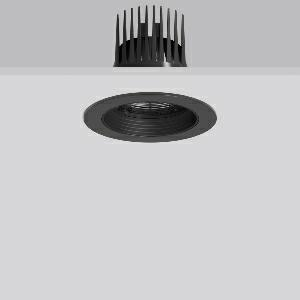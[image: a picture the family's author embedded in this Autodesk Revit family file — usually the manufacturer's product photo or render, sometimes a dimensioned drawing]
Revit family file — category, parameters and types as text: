
# Revit family: heledon_maxi_e_901768_003_2_8095
name_source: partatom
category: Lighting Fixtures
units: mm (PartAtom-declared; Revit-internal decimal feet)

## family parameters
Cut with Voids When Loaded = No
Host = Face
Light Source = No
Part Type = Normal
Room Calculation Point = No
Round Connector Dimension = Use Diameter
Shared = No

## types (1)
- HELEDON maxi E (1 x LED Modul 927, 3350 lm, 2700)
    Apparent Load = 35 VA
    Approval mark = CE
    CIE Flux Codes = 96 100 100 100 100
    Color Rendering = 92
    Color Temperature = 2700
    Default Elevation = 1800 mm
    Description = Series: HELEDON maxi
Round recessed downlight. Housing: die-cast aluminium, powder-coated. Black plastic ring and recessed LED to prevent glare from the side. Optical assembly with lens made of plastic (polycarbonate) for the best homogeneous light distribution - can be changed without tools. Best colour rendering index Ra>90. Suitable for Recessed ceiling mounting. Installation without tools thanks to spring fastening system. Including separate LED converter with connecting cable 600 mm.High quality converter without flickering and stroboscopic effect. Through-wiring box (5 pole) available as accessory. The following accessories can be mounted without use of tools: interchangeable lenses, decorative glasses, honeycomb louvre, clear and frosted diffusers, white interchangeable plastic ring. 
Colour: deep black, matt (RAL 9005)
Diameter: 162 mm
Height: 3 mm
Cut-out diameter: 152 mm
Recess height: 200 mm
Luminaire: recess height: 135 mm
Lamp: LED
Socket: without socket
Colour temperature: 2700K
Colour rendering index (CRI): 92
System power: 35 W
Rated luminous flux: 3350 lm
Luminous efficiency: 96 lm/W
Control gear: Regulated power supply
Protection class: II
Type of protection: IP 20
    Height = 0 mm  [stored 0 ft]
    Lamp = 1 x LED Modul 927
    Lamp Light Flux = 3350 lm
    Lamp count = 1
    Length = 162 mm
    Lifetime = 50000 h
    Luminous efficacy = 96 lm/W
    Manufacturer = RZB
    ModVariant = No
    Model = 901768.003.2
    Mounting Place = Ceiling
    Mounting Type = Recessed
    Number of Poles = 1
    OnlyDefault = Yes
    Power Factor = 1
    Product Name = HELEDON maxi E
    Product group = Recessed downlights
    ProductGroupID = 402
    Protection Class = Protection class II
    Protection Degree = IP 20
    RLX_Detail_Level = 1
    RLX_Emergency_Light_Flux = 0 lm
    RLX_Emergency_Type = 0
    RLX_Emergency_Type_DB = No
    RlxData = <blob elided: 122481 chars, md5=7da7b8e1>
    Socket = socket
    Standby Power = 0 W
    System Light Flux = 3350 lm
    System Power = 35 W
    Type Comments = Product without accessories
    Type Image = 901663.003.jpg
    URL = http://relux.com
    VarID = ---
    Voltage = 230 V
    Voltage Range = 220-240 V
    Weight = 0.00 kg
    Width = 0 mm  [stored 0 ft]

note: [stored X ft] marks values corroborated as IEEE doubles in the binary element streams (Revit-internal decimal feet)

## geometry (parser evidence)
native form markers: Blend x4, Sweep x11
no freeform markers — native parametric forms only
